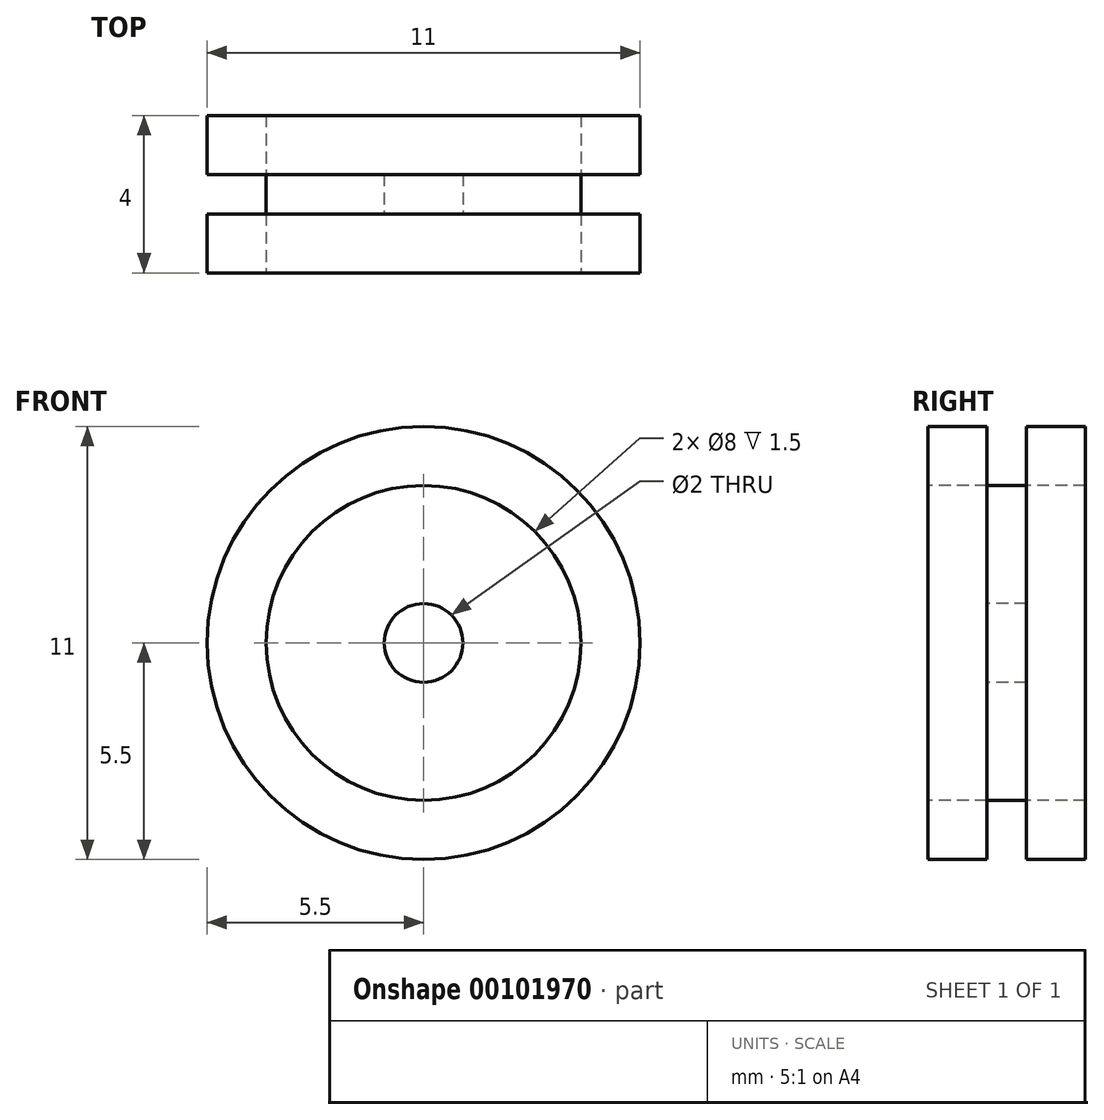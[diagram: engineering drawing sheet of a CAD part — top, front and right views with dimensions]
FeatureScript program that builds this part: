
annotation { "Feature Type Name" : "Feature", "Feature Type Description" : "" }
export const myFeature = defineFeature(function(context is Context, id is Id, definition is map)
    precondition{}
    {
        {
            var Q0;
            Q0=qCreatedBy(makeId("Right.planeOp"),FACE);
            var sketch = newSketch(context, id + "F0", { "sketchPlane" : qUnion([Q0])});
            skLineSegment(sketch, "E0", {"start": v(0, 0) * mm, "end": v(4, 0) * mm, "construction": true});
            skLineSegment(sketch, "E1.bottom", {"start": v(0, 1) * mm, "end": v(1.5, 1) * mm});
            skLineSegment(sketch, "E1.top", {"start": v(0, 5.5) * mm, "end": v(1.5, 5.5) * mm});
            skLineSegment(sketch, "E1.left", {"start": v(0, 1) * mm, "end": v(0, 5.5) * mm});
            skLineSegment(sketch, "E1.right", {"start": v(1.5, 1) * mm, "end": v(1.5, 5.5) * mm});
            skLineSegment(sketch, "E2.bottom", {"start": v(0, 1) * mm, "end": v(4, 1) * mm});
            skLineSegment(sketch, "E2.top", {"start": v(0, 4) * mm, "end": v(4, 4) * mm});
            skLineSegment(sketch, "E2.left", {"start": v(0, 1) * mm, "end": v(0, 4) * mm});
            skLineSegment(sketch, "E2.right", {"start": v(4, 1) * mm, "end": v(4, 4) * mm});
            skLineSegment(sketch, "E3.bottom", {"start": v(4, 1) * mm, "end": v(2.5, 1) * mm});
            skLineSegment(sketch, "E3.top", {"start": v(4, 5.5) * mm, "end": v(2.5, 5.5) * mm});
            skLineSegment(sketch, "E3.left", {"start": v(4, 1) * mm, "end": v(4, 5.5) * mm});
            skLineSegment(sketch, "E3.right", {"start": v(2.5, 1) * mm, "end": v(2.5, 5.5) * mm});
            skLineSegment(sketch, "E4.MirrorCS", {"start": v(4, -1) * mm, "end": v(4, -4) * mm});
            skLineSegment(sketch, "E5.MirrorCS", {"start": v(0, -1) * mm, "end": v(1.5, -1) * mm});
            skLineSegment(sketch, "E6.MirrorCS", {"start": v(0, -1) * mm, "end": v(4, -1) * mm});
            skLineSegment(sketch, "E7.MirrorCS", {"start": v(0, -4) * mm, "end": v(4, -4) * mm});
            skLineSegment(sketch, "E8.MirrorCS", {"start": v(0, -1) * mm, "end": v(0, -4) * mm});
            skLineSegment(sketch, "E9.MirrorCS", {"start": v(2.5, -1) * mm, "end": v(2.5, -5.5) * mm});
            skLineSegment(sketch, "E10.MirrorCS", {"start": v(4, -1) * mm, "end": v(4, -5.5) * mm});
            skLineSegment(sketch, "E11.MirrorCS", {"start": v(4, -5.5) * mm, "end": v(2.5, -5.5) * mm});
            skLineSegment(sketch, "E12.MirrorCS", {"start": v(4, -1) * mm, "end": v(2.5, -1) * mm});
            skLineSegment(sketch, "E13.MirrorCS", {"start": v(1.5, -1) * mm, "end": v(1.5, -5.5) * mm});
            skLineSegment(sketch, "E14.MirrorCS", {"start": v(0, -1) * mm, "end": v(0, -5.5) * mm});
            skLineSegment(sketch, "E15.MirrorCS", {"start": v(0, -5.5) * mm, "end": v(1.5, -5.5) * mm});
            skSolve(sketch);
        }
        {
            var Q0;
            {var subQ0=sQuery(id+"F0.wireOp",EDGE,"E2.bottom");var subQ1=sQuery(id+"F0.wireOp",EDGE,"E1.right");var subQ2=makeQuery(id+"F0.imprint","INTERSECT",VERTEX,{"derivedFrom":[subQ1,subQ0]});Q0=makeQuery(id+"F0.imprint","IMPRINT",FACE,{"disambiguationData":[TD([[makeQuery(id+"F0.imprint","IMPRINT",EDGE,{"disambiguationData":[TD([[subQ2,-1.0]])],"derivedFrom":subQ1}),-1.0]])]});}
            var Q1;
            {var subQ5=sQuery(id+"F0.wireOp",EDGE,"E3.bottom");Q1=makeQuery(id+"F0.imprint","IMPRINT",FACE,{"disambiguationData":[TD([[makeQuery(id+"F0.imprint","IMPRINT",EDGE,{"derivedFrom":subQ5}),-1.0]])]});}
            var Q2;
            {var subQ5=sQuery(id+"F0.wireOp",EDGE,"E3.top");Q2=makeQuery(id+"F0.imprint","IMPRINT",FACE,{"disambiguationData":[TD([[makeQuery(id+"F0.imprint","IMPRINT",EDGE,{"derivedFrom":subQ5}),1.0]])]});}
            var Q3;
            {var subQ0=sQuery(id+"F0.wireOp",EDGE,"E1.top");Q3=makeQuery(id+"F0.imprint","IMPRINT",FACE,{"disambiguationData":[TD([[makeQuery(id+"F0.imprint","IMPRINT",EDGE,{"derivedFrom":subQ0}),-1.0]])]});}
            var Q4;
            {var subQ5=sQuery(id+"F0.wireOp",EDGE,"E2.left");Q4=makeQuery(id+"F0.imprint","IMPRINT",FACE,{"disambiguationData":[TD([[makeQuery(id+"F0.imprint","IMPRINT",EDGE,{"derivedFrom":subQ5}),-1.0]])]});}
            var Q5;
            Q5=sQuery(id+"F0.wireOp",EDGE,"E0");
            revolve(context, id + "F1", {"entities" : qUnion([Q0, Q1, Q2, Q3, Q4]), "axis" : qUnion([Q5]), "revolveType" : RevolveType.FULL});
        }
    });
